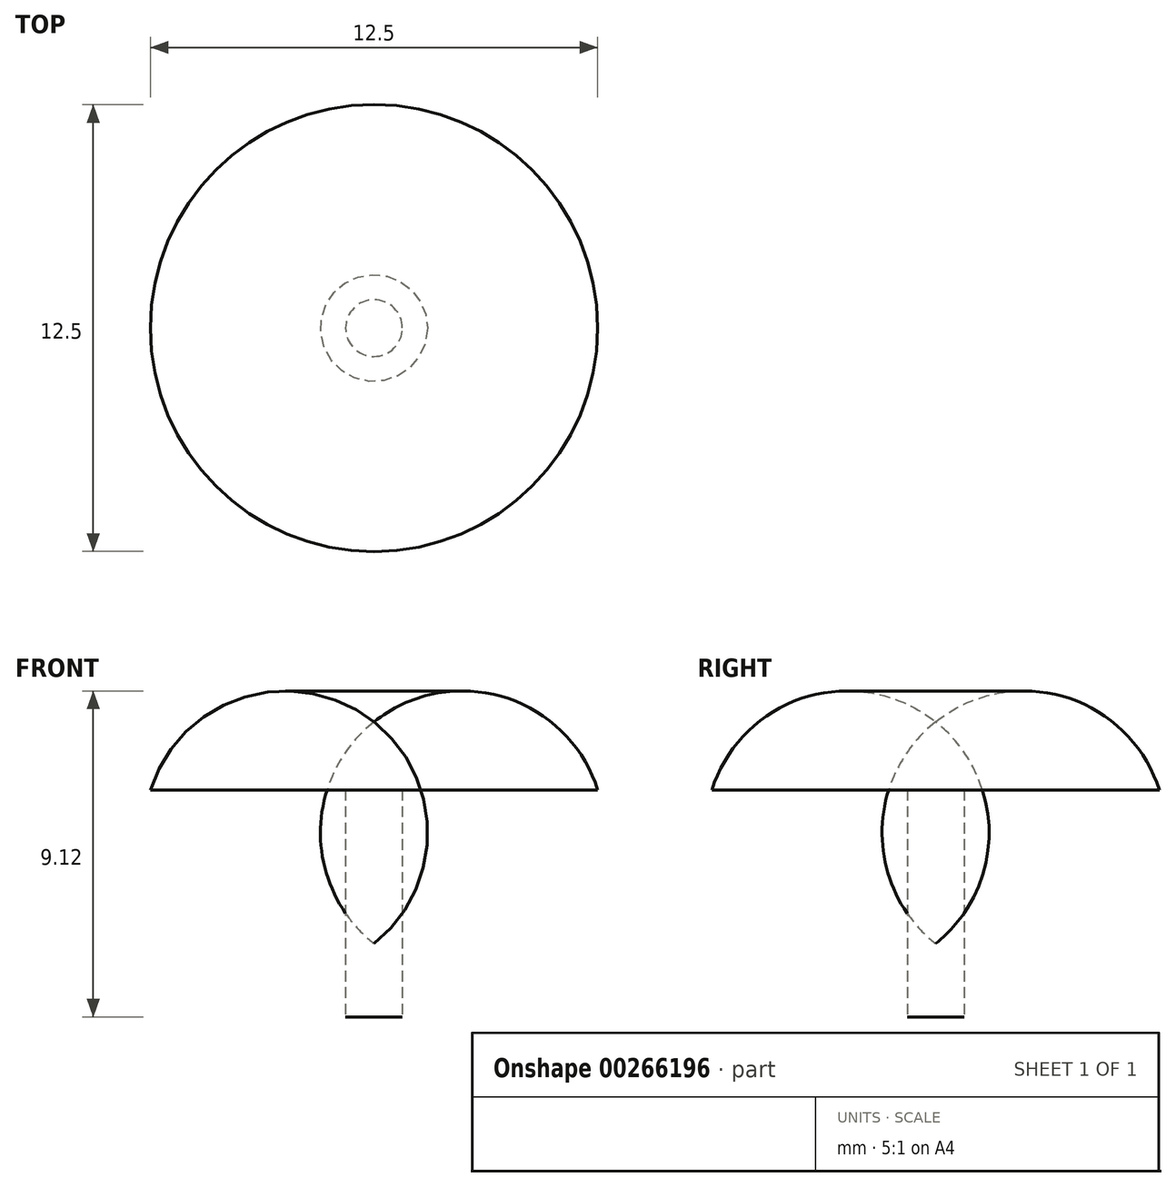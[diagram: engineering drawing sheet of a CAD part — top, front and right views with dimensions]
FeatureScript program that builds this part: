
annotation { "Feature Type Name" : "Feature", "Feature Type Description" : "" }
export const myFeature = defineFeature(function(context is Context, id is Id, definition is map)
    precondition{}
    {
        {
            var Q0;
            Q0=qCreatedBy(makeId("Front.planeOp"),FACE);
            var sketch = newSketch(context, id + "F0", { "sketchPlane" : qUnion([Q0])});
            skLineSegment(sketch, "E0", {"start": v(0, 0) * mm, "end": v(0, 8.26) * mm});
            skLineSegment(sketch, "E1", {"start": v(0, 0) * mm, "end": v(0.8, 0) * mm});
            skLineSegment(sketch, "E2", {"start": v(0.8, 0) * mm, "end": v(0.8, 6.35) * mm});
            skLineSegment(sketch, "E3", {"start": v(0.8, 6.35) * mm, "end": v(6.25, 6.35) * mm});
            skArc(sketch, "E4", {"start": v(6.25, 6.35) * mm, "mid": v(3.63, 8.95) * mm, "end": v(0, 8.26) * mm});
            skSolve(sketch);
        }
        {
            var Q0;
            Q0=makeQuery(id+"F0.imprint","IMPRINT",FACE,{"disambiguationData":[TD([[makeQuery(id+"F0.imprint","IMPRINT",EDGE,{"derivedFrom":sQuery(id+"F0.wireOp",EDGE,"E0")}),-1.0]])]});
            var Q1;
            Q1=sQuery(id+"F0.wireOp",EDGE,"E0");
            revolve(context, id + "F1", {"entities" : qUnion([Q0]), "axis" : qUnion([Q1]), "revolveType" : RevolveType.FULL});
        }
    });
